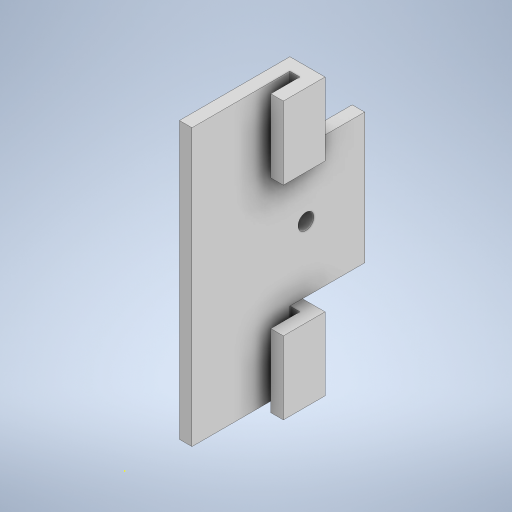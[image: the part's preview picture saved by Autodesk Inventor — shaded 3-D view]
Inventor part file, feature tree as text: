
AUTODESK INVENTOR PART (.ipt)
format: ipt  version: 2024.3 (Build 283343000, 343)  size: 320,000 bytes
history: native  units: in
note: dims shown in document units (in); Inventor stores cm internally (conversion verified against a paired STEP export)
features: sketch x8, extrude x7
ambient origin geometry x8: Origin, YZ Plane, XZ Plane, XY Plane, X Axis, Y Axis, Z Axis, Center Point
bodies: Solid1 (feature_tree)
feature tree (15):
  extrude  "Extrusion1"  Depth=0.2677in
  extrude  "Extrusion2"  Depth=0.0984in
  extrude  "Extrusion3"  Depth=0.2283in
  extrude  "Extrusion4"  Depth=0.2283in
  extrude  "Extrusion5"  Depth=0.5709in
  sketch  "Sketch6"  dims[d11=1.5551in d12=1.0236in d13=0.0in]
  extrude  "Extrusion6"  Depth=1.0236in TaperAngle=0.0deg
  extrude  "Extrusion7"  Depth=0.5709in
  sketch  "Sketch1"  dims[d0=2.1339in d1=0.2677in]
  sketch  "Sketch2"  dims[d2=0.3268in d3=0.0984in]
  sketch  "Sketch3"  dims[d4=0.2283in d5=0.0709in]
  sketch  "Sketch4"  dims[d6=0.3268in d7=0.2283in]
  sketch  "Sketch5"  dims[d8=0.5709in d9=0.0in d10=1.5551in]
  sketch  "Sketch7"  dims[d14=0.5709in d15=0.0in d18=0.5276in]
  sketch  "Sketch8"  dims[d19=0.1181in d20=0.1772in d21=0.0in d22=0.2283in d23=0.2283in d24=2.4562in d25=0.0in d26=2.4562in d27=0.0in d28=0.0276in d29=0.0in]
